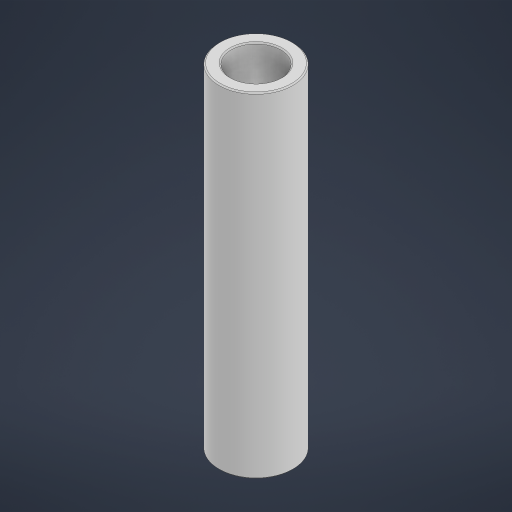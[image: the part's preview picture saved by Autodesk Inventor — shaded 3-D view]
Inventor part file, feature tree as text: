
AUTODESK INVENTOR PART (.ipt)
format: ipt  version: 2023 (Build 270158000, 158)  size: 177,664 bytes
history: native  units: in
note: dims shown in document units (in); Inventor stores cm internally (conversion verified against a paired STEP export)
features: chamfer x1
ambient origin geometry x8: Origin, YZ Plane, XZ Plane, XY Plane, X Axis, Y Axis, Z Axis, Center Point
bodies: Solid1 (feature_tree)
feature tree (1):
  chamfer  "Chamfer1"  [1 undecoded]
note: 1 required parameter value undecoded (feature->parameter linkage not recoverable at this tier; creation-order binding heuristic only, values carry confidence <= 0.55)
